# Revit family: METALFIRE_AVENUE_MF_1050-75_GHE_1S Brick
name_source: partatom
category: Mechanical Equipment
revit_build: Autodesk Revit 2018 (Build: 20190510_1515(x64)
units: mm (PartAtom-declared; Revit-internal decimal feet)

## family parameters
Always vertical = Yes
Cut with Voids When Loaded = No
Host = Wall
OmniClass Number = 23.75.00.00
OmniClass Title = Climate Control (HVAC)
Part Type = Normal
Room Calculation Point = No
Round Connector Dimension = Use Diameter
Shared = No

## types (1)
- MF_1050-750_GHE_1S Brick
    BIM BADGE = https://bim.archiproducts.com
    Description = The new AVENUE collection introduces meaningful and comprehensive innovations to the closed gas-burning Metalfire line-up.
    ENERGY EFFICIENCY CLASS = A (G20) / B (G30)
    FINISHING MATERIAL = Painted steel, cast iron
    FRAME MATERIAL = Iron - Metalfire
    HEIGHT = 740 mm
    MATERIAL DESCRIPTION = Iron, galvanized steel
    Manufacturer = METALFIRE
    Model = Avenue
    OUTPUT = 9500 W
    OVERALL DEPTH = 444 mm
    OVERALL HEIGHT = 1120 mm
    OVERALL WIDTH = 1178 mm
    PRODUCT CODE = MF 1050-75 GHE 1S Brick
    PRODUCT SHEET = https://www.archiproducts.com
    SMOKE EXHAUST = Ø130/200 mm
    TECHNICAL SHEET = https://www.metalfire.eu
    URL = https://www.metalfire.eu
    WEIGHT = 140.00 kg
    WIDTH = 1050 mm

## geometry (parser evidence)
native form markers: Blend x2, Sweep x5
no freeform markers — native parametric forms only
